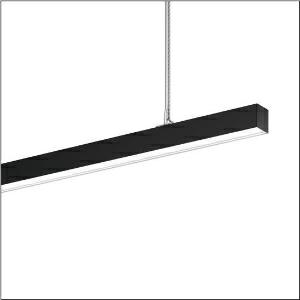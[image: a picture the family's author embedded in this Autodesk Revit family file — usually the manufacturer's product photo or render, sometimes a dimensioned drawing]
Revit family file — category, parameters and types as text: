
# Revit family: silica_r__21_51mx33da47bb_630a
name_source: partatom
category: Lighting Fixtures
units: mm (PartAtom-declared; Revit-internal decimal feet)

## family parameters
Cut with Voids When Loaded = No
Host = Face
Light Source = No
Part Type = Normal
Room Calculation Point = No
Round Connector Dimension = Use Diameter
Shared = No

## types (1)
- --- (1 x LED, 5910 lm, 38.4 W, 4000K)
    Apparent Load = 38 VA
    CIE Flux Codes = 78 96 99 55 100
    Color Rendering = 80
    Color Temperature = 4000K
    Default Elevation = 1800 mm
    Description = Silica® 21, office luminaire, primary optical cover: prismatic diffuser, of PMMA, CAT 2 (L<= 3000cd/m²), light emission: direct/indirect distribution, primary light characteristic: symmetric, installation type: suspended mounting, LED, rated luminous flux: 5.910lm, luminous efficacy: 154lm/W, light colour: 840, colour temperature: 4000K, with terminal, 3+2-pole, max. 2.5mm², mains connection: 220..240V, AC, 50/60Hz, rated input power: 38.4W, luminaire housing, of aluminium, jet black (RAL 9005), length: 1.204mm, width: 53mm, height: 53mm, protection rating (complete): IP20, insulation class (complete): insulation class I (protective earthing), certification: CE, permissible operating ambient temperature: 0..+35°C, standard: EN 50419, packaging unit: 1 piece
    Height = 53 mm
    Lamp = 1 x LED
    Lamp Light Flux = 5910 lm
    Lamp Power = 38.4 W
    Lamp count = 1
    Length = 1204 mm
    Luminous efficacy = 154 lm/W
    Manufacturer = Siteco
    ModVariant = No
    Model = 51MX33DA47BB
    Mounting Place = Ceiling
    Mounting Type = Pendant
    Number of Poles = 1
    OnlyDefault = Yes
    Power Factor = 1
    Product Name = Silica® 21
    Product group = office luminaire | ceiling pendant
    ProductGroupID = 902
    Protection Class = Protection class I
    Protection Degree = IP 20
    RLX_Detail_Level = 1
    RLX_Emergency_Light_Flux = 0 lm
    RLX_Emergency_Type = 0
    RLX_Emergency_Type_DB = No
    RlxData = <blob elided: 25929 chars, md5=9349734c>
    Socket = socket
    Standby Power = 0 W
    System Light Flux = 5910 lm
    System Power = 38 W
    Type Comments = factory setting: luminous flux: 100 % | dim-lin: 254 | 323 mA
    Type Image = l_1335856.jpg
    URL = http://relux.com
    VarID = @adj_087921
    Voltage = 0 V
    Weight = 0.00 kg
    Width = 53 mm

## geometry (parser evidence)
native form markers: Blend x4, Sweep x13
no freeform markers — native parametric forms only
